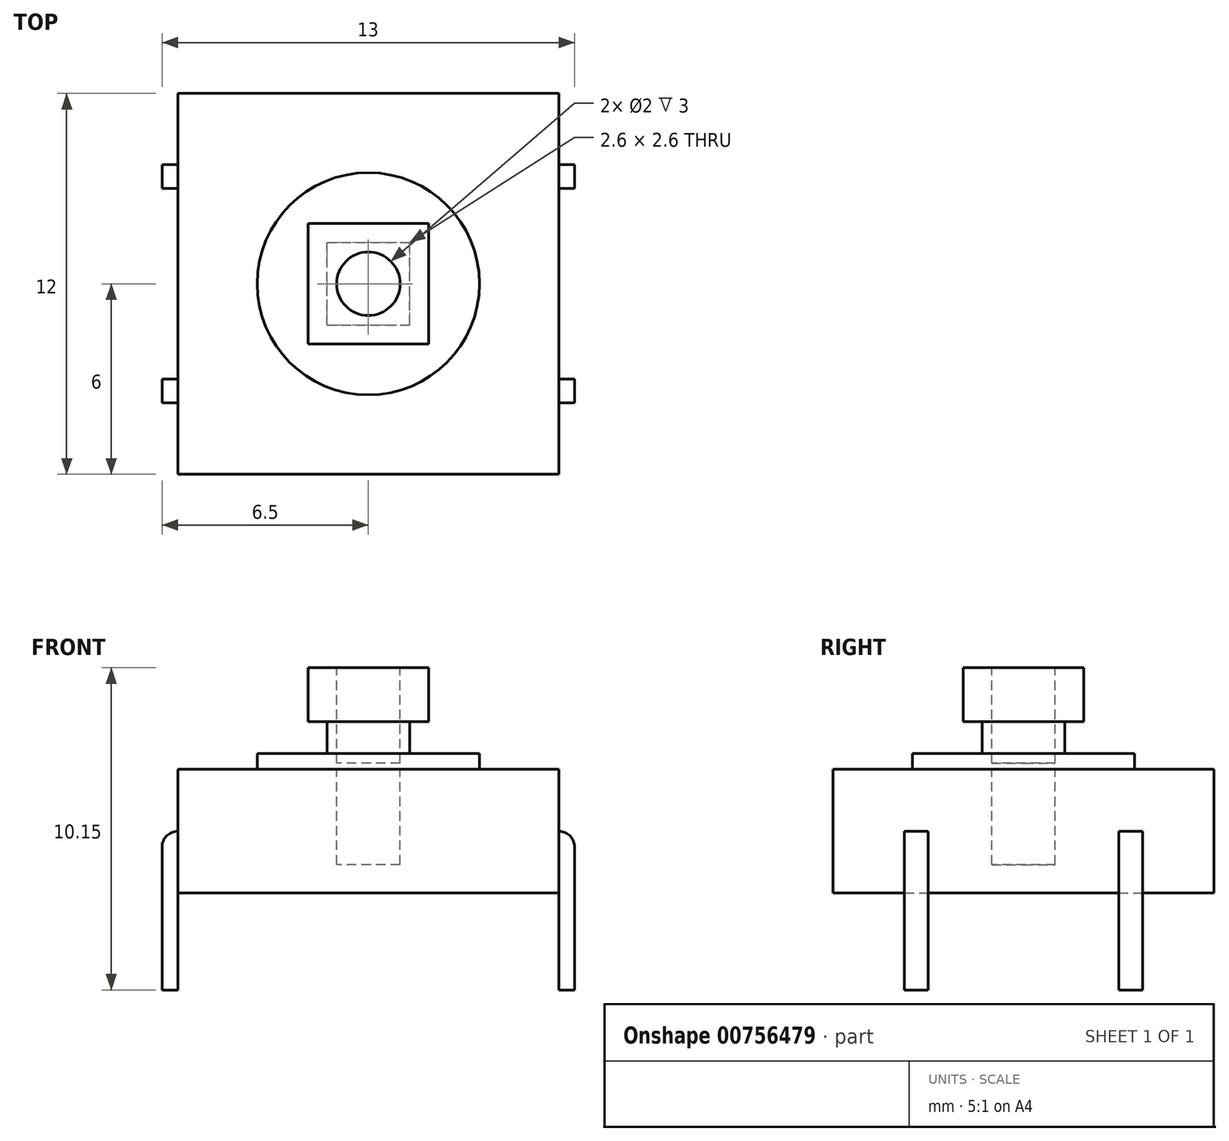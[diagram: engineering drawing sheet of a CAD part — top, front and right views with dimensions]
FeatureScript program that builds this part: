
annotation { "Feature Type Name" : "Feature", "Feature Type Description" : "" }
export const myFeature = defineFeature(function(context is Context, id is Id, definition is map)
    precondition{}
    {
        {
            var Q0;
            Q0=qCreatedBy(makeId("Top.planeOp"),FACE);
            var sketch = newSketch(context, id + "F0", { "sketchPlane" : qUnion([Q0])});
            skLineSegment(sketch, "E0.bottom", {"start": v(-6, -6) * mm, "end": v(6, -6) * mm});
            skLineSegment(sketch, "E0.top", {"start": v(-6, 6) * mm, "end": v(6, 6) * mm});
            skLineSegment(sketch, "E0.left", {"start": v(-6, -6) * mm, "end": v(-6, 6) * mm});
            skLineSegment(sketch, "E0.right", {"start": v(6, -6) * mm, "end": v(6, 6) * mm});
            skPoint(sketch, "E0.middle", {"position": v(0, 0) * mm});
            skCircle(sketch, "E1", {"center": v(0, 0) * mm, "radius": 3.5 * mm});
            skLineSegment(sketch, "E2.bottom", {"start": v(-1.9, -1.9) * mm, "end": v(1.9, -1.9) * mm});
            skLineSegment(sketch, "E2.top", {"start": v(-1.9, 1.9) * mm, "end": v(1.9, 1.9) * mm});
            skLineSegment(sketch, "E2.left", {"start": v(-1.9, -1.9) * mm, "end": v(-1.9, 1.9) * mm});
            skLineSegment(sketch, "E2.right", {"start": v(1.9, -1.9) * mm, "end": v(1.9, 1.9) * mm});
            skLineSegment(sketch, "E3.bottom", {"start": v(-1.3, -1.3) * mm, "end": v(1.3, -1.3) * mm});
            skLineSegment(sketch, "E3.top", {"start": v(-1.3, 1.3) * mm, "end": v(1.3, 1.3) * mm});
            skLineSegment(sketch, "E3.left", {"start": v(-1.3, -1.3) * mm, "end": v(-1.3, 1.3) * mm});
            skLineSegment(sketch, "E3.right", {"start": v(1.3, -1.3) * mm, "end": v(1.3, 1.3) * mm});
            skSolve(sketch);
        }
        {
            var Q0;
            Q0=makeQuery(id+"F0.imprint","IMPRINT",FACE,{"disambiguationData":[TD([[makeQuery(id+"F0.imprint","IMPRINT",EDGE,{"derivedFrom":sQuery(id+"F0.wireOp",EDGE,"E0.bottom")}),1.0]])]});
            var Q1;
            Q1=makeQuery(id+"F0.imprint","IMPRINT",FACE,{"disambiguationData":[TD([[makeQuery(id+"F0.imprint","IMPRINT",EDGE,{"derivedFrom":sQuery(id+"F0.wireOp",EDGE,"E1")}),1.0]])]});
            var Q2;
            Q2=makeQuery(id+"F0.imprint","IMPRINT",FACE,{"disambiguationData":[TD([[makeQuery(id+"F0.imprint","IMPRINT",EDGE,{"derivedFrom":sQuery(id+"F0.wireOp",EDGE,"E2.bottom")}),1.0]])]});
            var Q3;
            Q3=makeQuery(id+"F0.imprint","IMPRINT",FACE,{"disambiguationData":[TD([[makeQuery(id+"F0.imprint","IMPRINT",EDGE,{"derivedFrom":sQuery(id+"F0.wireOp",EDGE,"E3.bottom")}),1.0]])]});
            extrude(context, id + "F1", {"entities" : qUnion([Q0, Q1, Q2, Q3]), "oppositeDirection" : true, "depth" : 3.9 * mm, "offsetDistance" : 25 * mm});
        }
        {
            var Q0;
            Q0=makeQuery(id+"F0.imprint","IMPRINT",FACE,{"disambiguationData":[TD([[makeQuery(id+"F0.imprint","IMPRINT",EDGE,{"derivedFrom":sQuery(id+"F0.wireOp",EDGE,"E1")}),1.0]])]});
            var Q1;
            Q1=makeQuery(id+"F0.imprint","IMPRINT",FACE,{"disambiguationData":[TD([[makeQuery(id+"F0.imprint","IMPRINT",EDGE,{"derivedFrom":sQuery(id+"F0.wireOp",EDGE,"E2.bottom")}),1.0]])]});
            extrude(context, id + "F2", {"entities" : qUnion([Q0, Q1]), "operationType" : NewBodyOperationType.ADD, "depth" : .5 * mm, "offsetDistance" : 25 * mm});
        }
        {
            var Q0;
            Q0=makeQuery(id+"F0.imprint","IMPRINT",FACE,{"disambiguationData":[TD([[makeQuery(id+"F0.imprint","IMPRINT",EDGE,{"derivedFrom":sQuery(id+"F0.wireOp",EDGE,"E3.bottom")}),1.0]])]});
            extrude(context, id + "F3", {"entities" : qUnion([Q0]), "operationType" : NewBodyOperationType.ADD, "depth" : 1.5 * mm, "offsetDistance" : 25 * mm});
        }
        {
            var Q0;
            Q0=makeQuery(id+"F0.imprint","IMPRINT",FACE,{"disambiguationData":[TD([[makeQuery(id+"F0.imprint","IMPRINT",EDGE,{"derivedFrom":sQuery(id+"F0.wireOp",EDGE,"E0.bottom")}),1.0]])]});
            var sketch = newSketch(context, id + "F4", { "sketchPlane" : qUnion([Q0])});
            skPoint(sketch, "E4.0", {"position": v(0, 0) * mm});
            skCircle(sketch, "E5", {"center": v(0, 0) * mm, "radius": 1 * mm});
            skSolve(sketch);
        }
        {
            var Q0;
            Q0=makeQuery(id+"F4.imprint","IMPRINT",FACE,{"disambiguationData":[TD([[makeQuery(id+"F4.imprint","IMPRINT",EDGE,{"derivedFrom":sQuery(id+"F4.wireOp",EDGE,"E5")}),1.0]])]});
            extrude(context, id + "F5", {"entities" : qUnion([Q0]), "operationType" : NewBodyOperationType.REMOVE, "oppositeDirection" : true, "depth" : 3 * mm, "offsetDistance" : 25 * mm});
        }
        {
            var Q0;
            Q0=makeQuery(id+"F3.opExtrude","CAP_FACE",FACE,{"disambiguationData":[OSD([sQuery(id+"F0.wireOp",EDGE,"E3.bottom"),sQuery(id+"F0.wireOp",EDGE,"E3.top"),sQuery(id+"F0.wireOp",EDGE,"E3.left"),sQuery(id+"F0.wireOp",EDGE,"E3.right")])],"isStart":false});
            var sketch = newSketch(context, id + "F6", { "sketchPlane" : qUnion([Q0])});
            skLineSegment(sketch, "E6.0", {"start": v(-1.9, 1.9) * mm, "end": v(1.9, 1.9) * mm});
            skLineSegment(sketch, "E6.1", {"start": v(-1.9, -1.9) * mm, "end": v(-1.9, 1.9) * mm});
            skLineSegment(sketch, "E6.2", {"start": v(-1.9, -1.9) * mm, "end": v(1.9, -1.9) * mm});
            skLineSegment(sketch, "E6.3", {"start": v(1.9, -1.9) * mm, "end": v(1.9, 1.9) * mm});
            skSolve(sketch);
        }
        {
            var Q0;
            Q0=makeQuery(id+"F6.imprint","IMPRINT",FACE,{"disambiguationData":[TD([[makeQuery(id+"F6.imprint","IMPRINT",EDGE,{"derivedFrom":sQuery(id+"F6.wireOp",EDGE,"E6.0")}),-1.0]])]});
            var Q1;
            Q1=makeQuery(id+"F6.imprint","IMPRINT",FACE,{"disambiguationData":[TD([[makeQuery(id+"F6.imprint","IMPRINT",EDGE,{"derivedFrom":makeQuery(id+"F3.opExtrude","CAP_EDGE",EDGE,{"disambiguationData":[OSD([sQuery(id+"F0.wireOp",EDGE,"E3.bottom")])],"isStart":false})}),1.0]])]});
            extrude(context, id + "F7", {"entities" : qUnion([Q0, Q1]), "operationType" : NewBodyOperationType.ADD, "depth" : 1.7 * mm, "offsetDistance" : 25 * mm});
        }
        {
            var Q0;
            Q0=makeQuery(id+"F7.opExtrude","CAP_FACE",FACE,{"disambiguationData":[OSD([sQuery(id+"F6.wireOp",EDGE,"E6.0"),sQuery(id+"F6.wireOp",EDGE,"E6.1"),sQuery(id+"F6.wireOp",EDGE,"E6.2"),sQuery(id+"F6.wireOp",EDGE,"E6.3")])],"isStart":false});
            var sketch = newSketch(context, id + "F8", { "sketchPlane" : qUnion([Q0])});
            skCircle(sketch, "E7.0", {"center": v(0, 0) * mm, "radius": 1 * mm});
            skSolve(sketch);
        }
        {
            var Q0;
            Q0=makeQuery(id+"F8.imprint","IMPRINT",FACE,{"disambiguationData":[TD([[makeQuery(id+"F8.imprint","IMPRINT",EDGE,{"derivedFrom":sQuery(id+"F8.wireOp",EDGE,"E7.0")}),1.0]])]});
            extrude(context, id + "F9", {"entities" : qUnion([Q0]), "operationType" : NewBodyOperationType.REMOVE, "oppositeDirection" : true, "depth" : 3 * mm, "offsetDistance" : 25 * mm});
        }
        {
            var Q0;
            Q0=makeQuery(id+"F1.opExtrude","SWEPT_FACE",FACE,{"disambiguationData":[OSD([sQuery(id+"F0.wireOp",EDGE,"E0.right")])]});
            var sketch = newSketch(context, id + "F10", { "sketchPlane" : qUnion([Q0])});
            skLineSegment(sketch, "E8.0", {"start": v(-6, -3.9) * mm, "end": v(6, -3.9) * mm});
            skLineSegment(sketch, "E8.1", {"start": v(-6, -3.9) * mm, "end": v(-6, 0) * mm});
            skLineSegment(sketch, "E8.2", {"start": v(6, -3.9) * mm, "end": v(6, 0) * mm});
            skPoint(sketch, "E9.firstSnap0", {"position": v(-6, -1.95) * mm});
            skLineSegment(sketch, "E9.bottom", {"start": v(-3.75, -1.95) * mm, "end": v(-3, -1.95) * mm});
            skLineSegment(sketch, "E9.top", {"start": v(-3.75, -6.95) * mm, "end": v(-3, -6.95) * mm});
            skLineSegment(sketch, "E9.left", {"start": v(-3.75, -1.95) * mm, "end": v(-3.75, -6.95) * mm});
            skLineSegment(sketch, "E9.right", {"start": v(-3, -1.95) * mm, "end": v(-3, -6.95) * mm});
            skPoint(sketch, "E10", {"position": v(3.75, -1.95) * mm});
            skLineSegment(sketch, "E11.bottom", {"start": v(3, -1.95) * mm, "end": v(3.75, -1.95) * mm});
            skLineSegment(sketch, "E11.top", {"start": v(3, -6.95) * mm, "end": v(3.75, -6.95) * mm});
            skLineSegment(sketch, "E11.left", {"start": v(3, -1.95) * mm, "end": v(3, -6.95) * mm});
            skLineSegment(sketch, "E11.right", {"start": v(3.75, -1.95) * mm, "end": v(3.75, -6.95) * mm});
            skSolve(sketch);
        }
        {
            var Q0;
            Q0=makeQuery(id+"F1.opExtrude","SWEPT_FACE",FACE,{"disambiguationData":[OSD([sQuery(id+"F0.wireOp",EDGE,"E0.left")])]});
            var sketch = newSketch(context, id + "F11", { "sketchPlane" : qUnion([Q0])});
            skLineSegment(sketch, "E12.0", {"start": v(-6, -3.9) * mm, "end": v(-6, 0) * mm});
            skLineSegment(sketch, "E12.1", {"start": v(6, -3.9) * mm, "end": v(-6, -3.9) * mm});
            skLineSegment(sketch, "E12.2", {"start": v(6, -3.9) * mm, "end": v(6, 0) * mm});
            skLineSegment(sketch, "E12.3", {"start": v(-3.75, -1.95) * mm, "end": v(-3.75, -6.95) * mm});
            skLineSegment(sketch, "E12.4", {"start": v(-3, -1.95) * mm, "end": v(-3, -6.95) * mm});
            skLineSegment(sketch, "E12.5", {"start": v(-3, -6.95) * mm, "end": v(-3.75, -6.95) * mm});
            skLineSegment(sketch, "E12.6", {"start": v(-3, -1.95) * mm, "end": v(-3.75, -1.95) * mm});
            skLineSegment(sketch, "E12.7", {"start": v(3.75, -1.95) * mm, "end": v(3, -1.95) * mm});
            skLineSegment(sketch, "E12.8", {"start": v(3.75, -1.95) * mm, "end": v(3.75, -6.95) * mm});
            skLineSegment(sketch, "E12.9", {"start": v(3, -1.95) * mm, "end": v(3, -6.95) * mm});
            skLineSegment(sketch, "E12.10", {"start": v(3.75, -6.95) * mm, "end": v(3, -6.95) * mm});
            skSolve(sketch);
        }
        {
            var Q0;
            {var subQ5=sQuery(id+"F10.wireOp",EDGE,"E9.top");Q0=makeQuery(id+"F10.imprint","IMPRINT",FACE,{"disambiguationData":[TD([[makeQuery(id+"F10.imprint","IMPRINT",EDGE,{"derivedFrom":subQ5}),1.0]])]});}
            var Q1;
            {var subQ5=sQuery(id+"F10.wireOp",EDGE,"E9.bottom");Q1=makeQuery(id+"F10.imprint","IMPRINT",FACE,{"disambiguationData":[TD([[makeQuery(id+"F10.imprint","IMPRINT",EDGE,{"derivedFrom":subQ5}),-1.0]])]});}
            var Q2;
            {var subQ5=sQuery(id+"F10.wireOp",EDGE,"E11.top");Q2=makeQuery(id+"F10.imprint","IMPRINT",FACE,{"disambiguationData":[TD([[makeQuery(id+"F10.imprint","IMPRINT",EDGE,{"derivedFrom":subQ5}),1.0]])]});}
            var Q3;
            {var subQ5=sQuery(id+"F10.wireOp",EDGE,"E11.bottom");Q3=makeQuery(id+"F10.imprint","IMPRINT",FACE,{"disambiguationData":[TD([[makeQuery(id+"F10.imprint","IMPRINT",EDGE,{"derivedFrom":subQ5}),-1.0]])]});}
            extrude(context, id + "F12", {"entities" : qUnion([Q0, Q1, Q2, Q3]), "operationType" : NewBodyOperationType.ADD, "depth" : .5 * mm, "offsetDistance" : 25 * mm});
        }
        {
            var Q0;
            Q0=makeQuery(id+"F12.opExtrude","CAP_EDGE",EDGE,{"disambiguationData":[OSD([sQuery(id+"F10.wireOp",EDGE,"E9.bottom")])],"isStart":false});
            var Q1;
            Q1=makeQuery(id+"F12.opExtrude","CAP_EDGE",EDGE,{"disambiguationData":[OSD([sQuery(id+"F10.wireOp",EDGE,"E11.bottom")])],"isStart":false});
            fillet(context, id + "F13", {"entities" : qUnion([Q0, Q1]), "radius" : .5 * mm, "tangentPropagation" : true, "allowEdgeOverflow" : false});
        }
        {
            var Q0;
            {var subQ5=sQuery(id+"F11.wireOp",EDGE,"E12.7");Q0=makeQuery(id+"F11.imprint","IMPRINT",FACE,{"disambiguationData":[TD([[makeQuery(id+"F11.imprint","IMPRINT",EDGE,{"derivedFrom":subQ5}),1.0]])]});}
            var Q1;
            {var subQ5=sQuery(id+"F11.wireOp",EDGE,"E12.6");Q1=makeQuery(id+"F11.imprint","IMPRINT",FACE,{"disambiguationData":[TD([[makeQuery(id+"F11.imprint","IMPRINT",EDGE,{"derivedFrom":subQ5}),1.0]])]});}
            var Q2;
            {var subQ5=sQuery(id+"F11.wireOp",EDGE,"E12.5");Q2=makeQuery(id+"F11.imprint","IMPRINT",FACE,{"disambiguationData":[TD([[makeQuery(id+"F11.imprint","IMPRINT",EDGE,{"derivedFrom":subQ5}),-1.0]])]});}
            var Q3;
            {var subQ5=sQuery(id+"F11.wireOp",EDGE,"E12.10");Q3=makeQuery(id+"F11.imprint","IMPRINT",FACE,{"disambiguationData":[TD([[makeQuery(id+"F11.imprint","IMPRINT",EDGE,{"derivedFrom":subQ5}),-1.0]])]});}
            extrude(context, id + "F14", {"entities" : qUnion([Q0, Q1, Q2, Q3]), "operationType" : NewBodyOperationType.ADD, "depth" : .5 * mm, "offsetDistance" : 25 * mm});
        }
        {
            var Q0;
            Q0=makeQuery(id+"F14.opExtrude","CAP_EDGE",EDGE,{"disambiguationData":[OSD([sQuery(id+"F11.wireOp",EDGE,"E12.6")])],"isStart":false});
            var Q1;
            Q1=makeQuery(id+"F14.opExtrude","CAP_EDGE",EDGE,{"disambiguationData":[OSD([sQuery(id+"F11.wireOp",EDGE,"E12.7")])],"isStart":false});
            fillet(context, id + "F15", {"entities" : qUnion([Q0, Q1]), "radius" : .5 * mm, "tangentPropagation" : true, "allowEdgeOverflow" : false});
        }
    });
